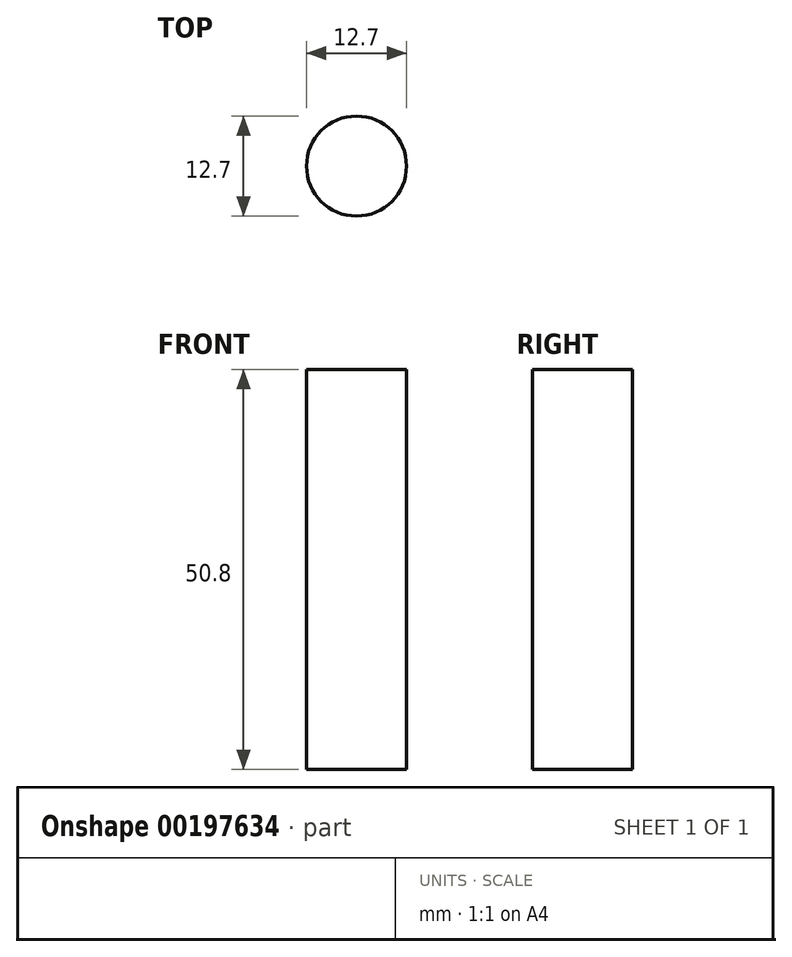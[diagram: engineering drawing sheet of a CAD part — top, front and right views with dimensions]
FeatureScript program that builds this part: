
annotation { "Feature Type Name" : "Feature", "Feature Type Description" : "" }
export const myFeature = defineFeature(function(context is Context, id is Id, definition is map)
    precondition{}
    {
        {
            var Q0;
            Q0=qCreatedBy(makeId("Top.planeOp"),FACE);
            var sketch = newSketch(context, id + "F0", { "sketchPlane" : qUnion([Q0])});
            skCircle(sketch, "E0", {"center": v(0, -0.52) * mm, "radius": 6.35 * mm});
            skSolve(sketch);
        }
        {
            var Q0;
            Q0=makeQuery(id+"F0.imprint","IMPRINT",FACE,{"disambiguationData":[TD([[makeQuery(id+"F0.imprint","IMPRINT",EDGE,{"derivedFrom":sQuery(id+"F0.wireOp",EDGE,"E0")}),1.0]])]});
            extrude(context, id + "F1", {"entities" : qUnion([Q0]), "depth" : 50.8 * mm});
        }
    });
